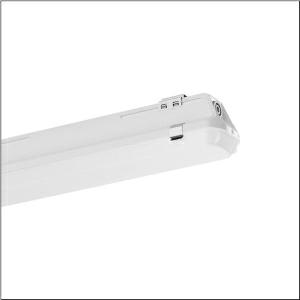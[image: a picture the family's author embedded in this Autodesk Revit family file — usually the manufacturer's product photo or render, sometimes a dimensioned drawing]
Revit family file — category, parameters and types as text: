
# Revit family: monsun_r__21_51fb207l447j3g_90a0
name_source: partatom
category: Lighting Fixtures
units: mm (PartAtom-declared; Revit-internal decimal feet)

## family parameters
Cut with Voids When Loaded = No
Host = Face
Light Source = No
Part Type = Normal
Room Calculation Point = No
Round Connector Dimension = Use Diameter
Shared = No

## types (1)
- --- (1 x LED, 760 lm, 4.5 W, 4000K)
    Apparent Load = 5 VA
    CIE Flux Codes = 45 75 93 94 100
    Color Rendering = 80
    Color Temperature = 4000K
    Default Elevation = 1800 mm
    Description = Monsun® 21, damp-proof luminaire, chain hanger, primary optical cover: enclosure, of PC, light emission: direct distribution, primary light characteristic: symmetric, installation type: suspended mounting, surface-mounted, horizontal mounting, vertical mounting, LED, rated luminous flux: 4.320lm, luminous efficacy: 127lm/W, light colour: 840, colour temperature: 4000K, control gear: ECG, with terminal, 3-pole, max. 2.5mm², mains connection: 220..240V, AC, 50/60Hz, rated input power: 34W, control gear: single battery element, battery: NiCd, 4,5Ah, mains connection: 230V, housing, of glass-fibre reinforced plastic, uncoated, bright grey, incl. chain hanger, length: 1.299mm, width: 90mm, height: 88mm, clip for enclosure, of stainless steel (V2A), ceiling mounting element, of stainless steel (V2A), chain hanger, of stainless steel (V2A), protection rating (complete): IP66, insulation class (complete): insulation class I (protective earthing), certification: CE, UKCA, protection symbol: D, impact resistance: IK08, permissible operating ambient temperature: +5..+25°C, standard: EN 50419, EN 60598-2-1, corresponds to IFS (International Featured Standards) requirements for safety and quality in the food industry, for indoor or canopied outdoor use, no direct snow, no direct sun, no direct rain, contact your sales advisor before using the luminaires in applications with unclear chemical exposure, large temperature fluctuations or condensation-forming humidity, LABS conformity tested according to VDMA 24364:2018-05, packaging unit: 1 piece
    Height = 88 mm
    Lamp = 1 x LED
    Lamp Light Flux = 760 lm
    Lamp Power = 4.5 W
    Lamp count = 1
    Length = 1299 mm
    Luminous efficacy = 169 lm/W
    Manufacturer = Siteco
    ModVariant = No
    Model = 51FB207L447J3G
    Mounting Place = Ceiling
    Mounting Type = Surface mounted
    Number of Poles = 1
    OnlyDefault = Yes
    Power Factor = 1
    Product Name = Monsun® 21
    Product group = damp-proof luminaire
    ProductGroupID = 300
    Protection Class = Protection class I
    Protection Degree = IP 66
    RLX_Detail_Level = 1
    RLX_Emergency_Light_Flux = 0 lm
    RLX_Emergency_Type = 0
    RLX_Emergency_Type_DB = No
    RlxData = <blob elided: 89973 chars, md5=09618173>
    Socket = socket
    Standby Power = 0 W
    System Light Flux = 760 lm
    System Power = 5 W
    Type Comments = : 3 h
    Type Image = l_1006717.jpg
    URL = http://relux.com
    VarID = @adj_074881
    Voltage = 0 V
    Weight = 0.00 kg
    Width = 90 mm

## geometry (parser evidence)
native form markers: Blend x4, Sweep x12
no freeform markers — native parametric forms only
